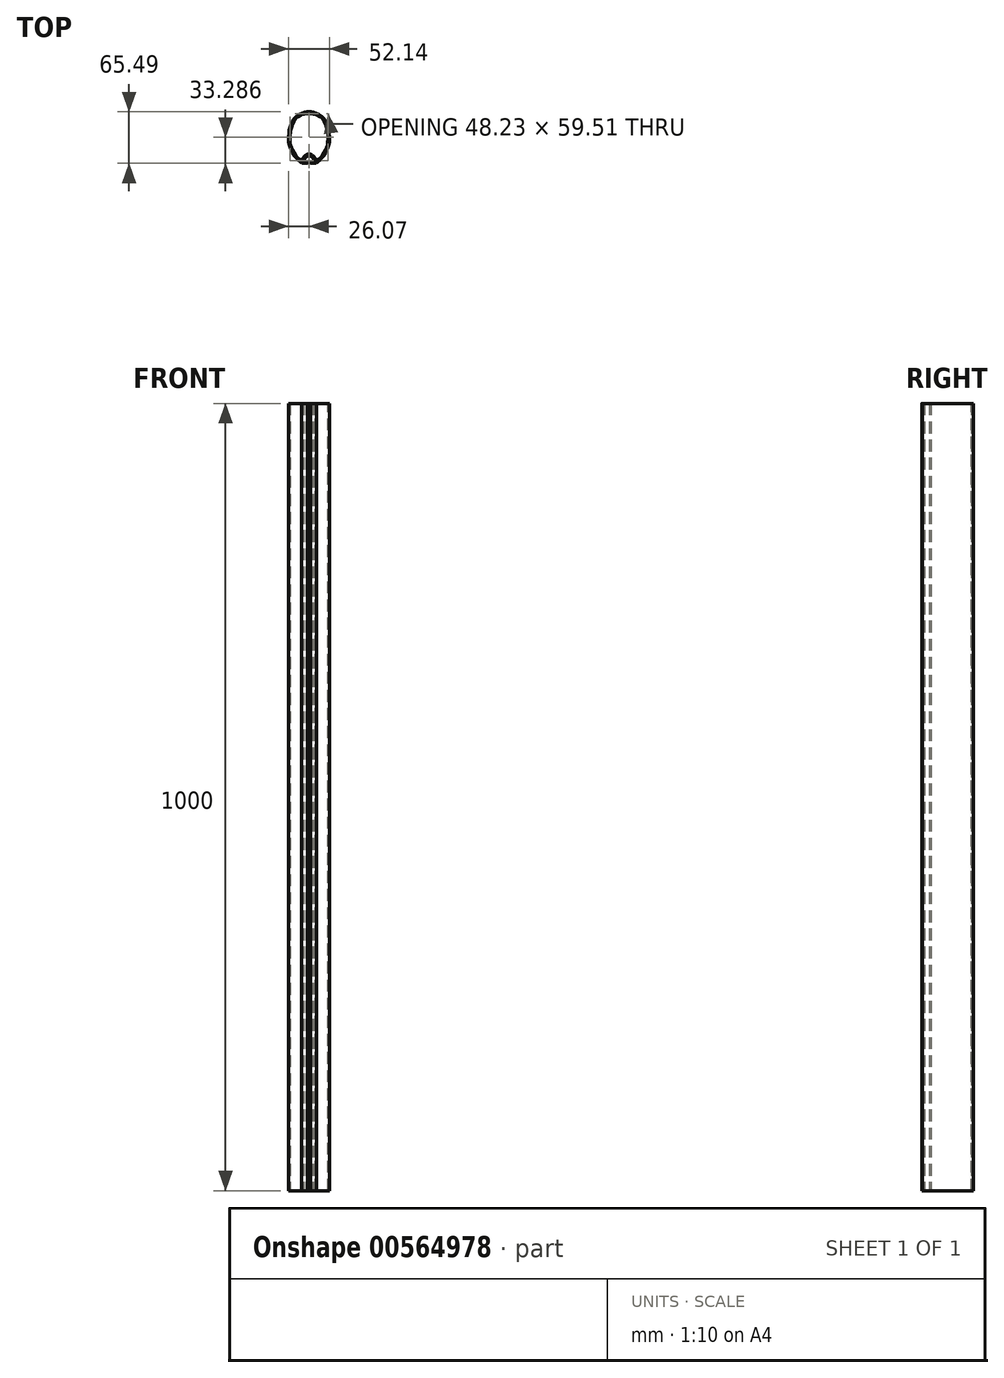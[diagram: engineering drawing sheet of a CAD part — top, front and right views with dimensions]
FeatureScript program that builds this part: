
annotation { "Feature Type Name" : "Feature", "Feature Type Description" : "" }
export const myFeature = defineFeature(function(context is Context, id is Id, definition is map)
    precondition{}
    {
        {
            var Q0;
            Q0=qCreatedBy(makeId("Top.planeOp"),FACE);
            var sketch = newSketch(context, id + "F0", { "sketchPlane" : qUnion([Q0])});
            skPoint(sketch, "E0", {"position": v(0, 8.5) * mm});
            skSolve(sketch);
        }
        {
            var Q0;
            Q0=qCreatedBy(makeId("Top.planeOp"),FACE);
            var sketch = newSketch(context, id + "F1", { "sketchPlane" : qUnion([Q0])});
            skPoint(sketch, "E1", {"position": v(0, -1.5) * mm});
            skSolve(sketch);
        }
        {
            var Q0;
            Q0=qCreatedBy(makeId("Top.planeOp"),FACE);
            var sketch = newSketch(context, id + "F2", { "sketchPlane" : qUnion([Q0])});
            skPoint(sketch, "E2", {"position": v(-13, 0) * mm});
            skSolve(sketch);
        }
        {
            var Q0;
            Q0=qCreatedBy(makeId("Top.planeOp"),FACE);
            var sketch = newSketch(context, id + "F3", { "sketchPlane" : qUnion([Q0])});
            skPoint(sketch, "E3", {"position": v(-20.75, 0) * mm});
            skSolve(sketch);
        }
        {
            var Q0;
            Q0=qCreatedBy(makeId("Top.planeOp"),FACE);
            var sketch = newSketch(context, id + "F4", { "sketchPlane" : qUnion([Q0])});
            skLineSegment(sketch, "E4", {"start": v(-20.75, 0) * mm, "end": v(-20.75, 0.34) * mm});
            skSolve(sketch);
        }
        {
            var Q0;
            Q0=qCreatedBy(makeId("Top.planeOp"),FACE);
            var sketch = newSketch(context, id + "F5", { "sketchPlane" : qUnion([Q0])});
            skPoint(sketch, "E5", {"position": v(-20.75, 0.34) * mm});
            skSolve(sketch);
        }
        {
            var Q0;
            Q0=qCreatedBy(makeId("Top.planeOp"),FACE);
            var sketch = newSketch(context, id + "F6", { "sketchPlane" : qUnion([Q0])});
            skPoint(sketch, "E6", {"position": v(0, -32.5) * mm});
            skSolve(sketch);
        }
        {
            var Q0;
            Q0=qCreatedBy(makeId("Top.planeOp"),FACE);
            var sketch = newSketch(context, id + "F7", { "sketchPlane" : qUnion([Q0])});
            skPoint(sketch, "E7", {"position": v(0, -22.83) * mm});
            skSolve(sketch);
        }
        {
            var Q0;
            Q0=qCreatedBy(makeId("Top.planeOp"),FACE);
            var sketch = newSketch(context, id + "F8", { "sketchPlane" : qUnion([Q0])});
            skPoint(sketch, "E8", {"position": v(0, -27.83) * mm});
            skSolve(sketch);
        }
        {
            var Q0;
            Q0=qCreatedBy(makeId("Top.planeOp"),FACE);
            var sketch = newSketch(context, id + "F9", { "sketchPlane" : qUnion([Q0])});
            skCircle(sketch, "E9", {"center": v(0, -27.83) * mm, "radius": 5 * mm});
            skSolve(sketch);
        }
        {
            var Q0;
            Q0=qCreatedBy(makeId("Top.planeOp"),FACE);
            var sketch = newSketch(context, id + "F10", { "sketchPlane" : qUnion([Q0])});
            skCircle(sketch, "E10", {"center": v(0, -27.83) * mm, "radius": 7.25 * mm});
            skSolve(sketch);
        }
        {
            var Q0;
            Q0=qCreatedBy(makeId("Top.planeOp"),FACE);
            var sketch = newSketch(context, id + "F11", { "sketchPlane" : qUnion([Q0])});
            skLineSegment(sketch, "E11", {"start": v(-2.11, -14.04) * mm, "end": v(17.17, -37.02) * mm});
            skSolve(sketch);
        }
        {
            var Q0;
            Q0=qCreatedBy(makeId("Top.planeOp"),FACE);
            var sketch = newSketch(context, id + "F12", { "sketchPlane" : qUnion([Q0])});
            skLineSegment(sketch, "E12", {"start": v(-4.06, -15.22) * mm, "end": v(15.2, -38.17) * mm});
            skSolve(sketch);
        }
        {
            var Q0;
            Q0=qCreatedBy(makeId("Top.planeOp"),FACE);
            var sketch = newSketch(context, id + "F13", { "sketchPlane" : qUnion([Q0])});
            skPoint(sketch, "E13", {"position": v(3.83, -24.62) * mm});
            skSolve(sketch);
        }
        {
            var Q0;
            Q0=qCreatedBy(makeId("Top.planeOp"),FACE);
            var sketch = newSketch(context, id + "F14", { "sketchPlane" : qUnion([Q0])});
            skPoint(sketch, "E14", {"position": v(5.55, -23.17) * mm});
            skSolve(sketch);
        }
        {
            var Q0;
            Q0=qCreatedBy(makeId("Top.planeOp"),FACE);
            var sketch = newSketch(context, id + "F15", { "sketchPlane" : qUnion([Q0])});
            skPoint(sketch, "E15", {"position": v(0, -20.58) * mm});
            skSolve(sketch);
        }
        {
            var Q0;
            Q0=qCreatedBy(makeId("Top.planeOp"),FACE);
            var sketch = newSketch(context, id + "F16", { "sketchPlane" : qUnion([Q0])});
            skArc(sketch, "E16", {"start": v(0, -20.58) * mm, "mid": v(3.06, -21.26) * mm, "end": v(5.55, -23.17) * mm});
            skSolve(sketch);
        }
        {
            var Q0;
            Q0=qCreatedBy(makeId("Top.planeOp"),FACE);
            var sketch = newSketch(context, id + "F17", { "sketchPlane" : qUnion([Q0])});
            skArc(sketch, "E17", {"start": v(0, -22.83) * mm, "mid": v(2.11, -23.3) * mm, "end": v(3.83, -24.62) * mm});
            skSolve(sketch);
        }
        {
            var Q0;
            Q0=qCreatedBy(makeId("Top.planeOp"),FACE);
            var sketch = newSketch(context, id + "F18", { "sketchPlane" : qUnion([Q0])});
            skLineSegment(sketch, "E18", {"start": v(0, -20.58) * mm, "end": v(0, -22.83) * mm});
            skSolve(sketch);
        }
        {
            var Q0;
            Q0=qCreatedBy(makeId("Top.planeOp"),FACE);
            var sketch = newSketch(context, id + "F19", { "sketchPlane" : qUnion([Q0])});
            skPoint(sketch, "E19", {"position": v(0, 33) * mm});
            skSolve(sketch);
        }
        {
            var Q0;
            Q0=qCreatedBy(makeId("Top.planeOp"),FACE);
            var sketch = newSketch(context, id + "F20", { "sketchPlane" : qUnion([Q0])});
            skCircle(sketch, "E20", {"center": v(-13, 0) * mm, "radius": 37.25 * mm});
            skSolve(sketch);
        }
        {
            var Q0;
            Q0=qCreatedBy(makeId("Top.planeOp"),FACE);
            var sketch = newSketch(context, id + "F21", { "sketchPlane" : qUnion([Q0])});
            skPoint(sketch, "E21", {"position": v(8.62, -30.33) * mm});
            skSolve(sketch);
        }
        {
            var Q0;
            Q0=qCreatedBy(makeId("Top.planeOp"),FACE);
            var sketch = newSketch(context, id + "F22", { "sketchPlane" : qUnion([Q0])});
            skPoint(sketch, "E22", {"position": v(10.42, -28.97) * mm});
            skSolve(sketch);
        }
        {
            var Q0;
            Q0=qCreatedBy(makeId("Top.planeOp"),FACE);
            var sketch = newSketch(context, id + "F23", { "sketchPlane" : qUnion([Q0])});
            skPoint(sketch, "E23", {"position": v(6.65, -26.5) * mm});
            skSolve(sketch);
        }
        {
            var Q0;
            Q0=qCreatedBy(makeId("Top.planeOp"),FACE);
            var sketch = newSketch(context, id + "F24", { "sketchPlane" : qUnion([Q0])});
            skLineSegment(sketch, "E24.bottom", {"start": v(0, -32.5) * mm, "end": v(1.75, -32.5) * mm});
            skLineSegment(sketch, "E24.top", {"start": v(0, -31) * mm, "end": v(1.75, -31) * mm});
            skLineSegment(sketch, "E24.left", {"start": v(0, -32.5) * mm, "end": v(0, -31) * mm});
            skLineSegment(sketch, "E24.right", {"start": v(1.75, -32.5) * mm, "end": v(1.75, -31) * mm});
            skSolve(sketch);
        }
        {
            var Q0;
            Q0=qCreatedBy(makeId("Top.planeOp"),FACE);
            var sketch = newSketch(context, id + "F25", { "sketchPlane" : qUnion([Q0])});
            skLineSegment(sketch, "E25.bottom", {"start": v(1.75, -32.5) * mm, "end": v(6.65, -32.5) * mm});
            skLineSegment(sketch, "E25.top", {"start": v(1.75, -31) * mm, "end": v(6.65, -31) * mm});
            skLineSegment(sketch, "E25.left", {"start": v(1.75, -32.5) * mm, "end": v(1.75, -31) * mm});
            skLineSegment(sketch, "E25.right", {"start": v(6.65, -32.5) * mm, "end": v(6.65, -31) * mm});
            skSolve(sketch);
        }
        {
            var Q0;
            Q0=qCreatedBy(makeId("Top.planeOp"),FACE);
            var sketch = newSketch(context, id + "F26", { "sketchPlane" : qUnion([Q0])});
            skArc(sketch, "E26", {"start": v(9.68, -31.68) * mm, "mid": v(8.22, -32.3) * mm, "end": v(6.65, -32.5) * mm});
            skSolve(sketch);
        }
        {
            var Q0;
            Q0=qCreatedBy(makeId("Top.planeOp"),FACE);
            var sketch = newSketch(context, id + "F27", { "sketchPlane" : qUnion([Q0])});
            skFitSpline(sketch, "E27", {"points": [v(10.42, -28.97) * mm, v(14.17, -25.46) * mm, v(16.96, -22.08) * mm, v(19.62, -17.98) * mm, v(21.39, -14.28) * mm, v(22.82, -10.41) * mm, v(23.66, -6.65) * mm, v(24.1, -3.42) * mm, v(24.24, 0) * mm, v(24.09, 3.46) * mm, v(23.7, 6.94) * mm, v(22.76, 11.67) * mm, v(21.35, 16.22) * mm, v(19.88, 19.59) * mm, v(16.38, 24.28) * mm, v(13.4, 26.83) * mm, v(10.3, 28.77) * mm, v(9.78, 28.98) * mm, v(9.04, 29.21) * mm, v(4.04, 30.3) * mm, v(0, 30.54) * mm], "startDerivative": vector(65.68, 55.9) * mm, "endDerivative": vector(-74.77, 3.53) * mm});
            skSolve(sketch);
        }
        {
            var Q0;
            Q0=qCreatedBy(makeId("Top.planeOp"),FACE);
            var sketch = newSketch(context, id + "F28", { "sketchPlane" : qUnion([Q0])});
            skFitSpline(sketch, "E28", {"points": [v(9.68, -31.68) * mm, v(10.28, -31.25) * mm, v(11.63, -30.22) * mm, v(15.66, -26.5) * mm, v(18.52, -23) * mm, v(21.18, -18.81) * mm, v(23.06, -14.82) * mm, v(24.5, -10.77) * mm, v(25.41, -6.88) * mm, v(25.87, -3.56) * mm, v(26, 0) * mm, v(25.84, 3.56) * mm, v(25.45, 7.22) * mm, v(24.5, 11.98) * mm, v(23.06, 16.71) * mm, v(21.46, 20.28) * mm, v(17.69, 25.4) * mm, v(14.4, 28.3) * mm, v(10.61, 30.57) * mm, v(7.6, 31.76) * mm, v(3.98, 32.66) * mm, v(0, 33) * mm], "startDerivative": vector(25.9, 18.75) * mm, "endDerivative": vector(-83.26, 2.5) * mm});
            skSolve(sketch);
        }
        {
            var Q0;
            Q0=qCreatedBy(makeId("Top.planeOp"),FACE);
            var sketch = newSketch(context, id + "F29", { "sketchPlane" : qUnion([Q0])});
            skLineSegment(sketch, "E29", {"start": v(8.62, -30.33) * mm, "end": v(3.83, -24.62) * mm});
            skSolve(sketch);
        }
        {
            var Q0;
            Q0=qCreatedBy(makeId("Top.planeOp"),FACE);
            var sketch = newSketch(context, id + "F30", { "sketchPlane" : qUnion([Q0])});
            skLineSegment(sketch, "E30", {"start": v(5.55, -23.17) * mm, "end": v(10.42, -28.97) * mm});
            skSolve(sketch);
        }
        {
            var Q0;
            Q0=qCreatedBy(makeId("Top.planeOp"),FACE);
            var sketch = newSketch(context, id + "F31", { "sketchPlane" : qUnion([Q0])});
            skPoint(sketch, "E31", {"position": v(2.75, -31.5) * mm});
            skSolve(sketch);
        }
        {
            var Q0;
            Q0=qCreatedBy(makeId("Top.planeOp"),FACE);
            var sketch = newSketch(context, id + "F32", { "sketchPlane" : qUnion([Q0])});
            skArc(sketch, "E32", {"start": v(2.75, -32.5) * mm, "mid": v(1.88, -31) * mm, "end": v(3.62, -31) * mm});
            skSolve(sketch);
        }
        {
            var Q0;
            Q0=qCreatedBy(makeId("Top.planeOp"),FACE);
            var sketch = newSketch(context, id + "F33", { "sketchPlane" : qUnion([Q0])});
            skFitSpline(sketch, "E33", {"points": [v(6.65, -31) * mm, v(7.55, -30.97) * mm, v(8.25, -30.82) * mm, v(8.52, -30.56) * mm, v(8.47, -30.14) * mm], "startDerivative": vector(2.94, 0.03) * mm, "endDerivative": vector(-1.7, 2.33) * mm});
            skSolve(sketch);
        }
        {
            var Q0;
            Q0=qCreatedBy(makeId("Top.planeOp"),FACE);
            var sketch = newSketch(context, id + "F34", { "sketchPlane" : qUnion([Q0])});
            skLineSegment(sketch, "E34", {"start": v(2.75, -32.5) * mm, "end": v(6.65, -32.5) * mm});
            skSolve(sketch);
        }
        {
            var Q0;
            Q0=qCreatedBy(makeId("Top.planeOp"),FACE);
            var sketch = newSketch(context, id + "F35", { "sketchPlane" : qUnion([Q0])});
            skLineSegment(sketch, "E35", {"start": v(3.62, -31) * mm, "end": v(6.65, -31) * mm});
            skSolve(sketch);
        }
        {
            var Q0;
            Q0=qCreatedBy(makeId("Top.planeOp"),FACE);
            var sketch = newSketch(context, id + "F36", { "sketchPlane" : qUnion([Q0])});
            skLineSegment(sketch, "E36", {"start": v(0, 33) * mm, "end": v(0, 30.54) * mm});
            skSolve(sketch);
        }
        {
            var Q0;
            Q0=qCreatedBy(makeId("Top.planeOp"),FACE);
            var sketch = newSketch(context, id + "F37", { "sketchPlane" : qUnion([Q0])});
            skLineSegment(sketch, "E37", {"start": v(23.55, 7.92) * mm, "end": v(23.55, -7.26) * mm});
            skSolve(sketch);
        }
        {
            var Q0;
            Q0=qCreatedBy(makeId("Top.planeOp"),FACE);
            var sketch = newSketch(context, id + "F38", { "sketchPlane" : qUnion([Q0])});
            skLineSegment(sketch, "E38.0", {"start": v(23.55, 7.92) * mm, "end": v(23.55, -7.26) * mm});
            skArc(sketch, "E39.0", {"start": v(0, -20.58) * mm, "mid": v(3.06, -21.26) * mm, "end": v(5.55, -23.17) * mm});
            skLineSegment(sketch, "E40.0", {"start": v(5.55, -23.17) * mm, "end": v(10.42, -28.97) * mm});
            skFitSpline(sketch, "E41.0", {"points": [v(10.42, -28.97) * mm, v(11.7, -27.87) * mm, v(14.28, -25.52) * mm, v(16.99, -22.17) * mm, v(19.73, -18.03) * mm, v(21.4, -14.32) * mm, v(22.92, -10.47) * mm, v(23.7, -6.67) * mm, v(24.15, -3.44) * mm, v(24.29, 0) * mm, v(24.11, 3.5) * mm, v(23.76, 6.99) * mm, v(22.88, 11.68) * mm, v(21.35, 16.27) * mm, v(20.12, 19.63) * mm, v(16.44, 24.51) * mm, v(13.71, 26.7) * mm, v(10.38, 28.8) * mm, v(9.77, 28.98) * mm, v(8.94, 29.28) * mm, v(3.79, 30.55) * mm, v(1.3, 30.48) * mm, v(0, 30.54) * mm]});
            skFitSpline(sketch, "E42.0", {"points": [v(9.68, -31.68) * mm, v(9.86, -31.55) * mm, v(10.36, -31.2) * mm, v(11.77, -30.18) * mm, v(15.9, -26.46) * mm, v(18.51, -23.1) * mm, v(21.3, -18.85) * mm, v(23.1, -14.87) * mm, v(24.58, -10.82) * mm, v(25.46, -6.9) * mm, v(25.93, -3.58) * mm, v(26.06, 0.01) * mm, v(25.85, 3.6) * mm, v(25.51, 7.28) * mm, v(24.6, 11.99) * mm, v(23.08, 16.79) * mm, v(21.68, 20.33) * mm, v(17.79, 25.62) * mm, v(14.6, 28.3) * mm, v(10.65, 30.68) * mm, v(7.64, 31.8) * mm, v(3.96, 32.8) * mm, v(1.34, 32.95) * mm, v(0, 33) * mm]});
            skArc(sketch, "E43.0", {"start": v(9.68, -31.68) * mm, "mid": v(8.22, -32.3) * mm, "end": v(6.65, -32.5) * mm});
            skLineSegment(sketch, "E44.0", {"start": v(2.75, -32.5) * mm, "end": v(6.65, -32.5) * mm});
            skArc(sketch, "E45.0", {"start": v(2.75, -32.5) * mm, "mid": v(1.88, -31) * mm, "end": v(3.62, -31) * mm});
            skLineSegment(sketch, "E46.0", {"start": v(3.62, -31) * mm, "end": v(6.65, -31) * mm});
            skFitSpline(sketch, "E47.0", {"points": [v(6.65, -31) * mm, v(6.95, -31) * mm, v(7.52, -30.99) * mm, v(8.25, -30.88) * mm, v(8.57, -30.58) * mm, v(8.59, -30.3) * mm, v(8.47, -30.14) * mm]});
            skLineSegment(sketch, "E48.0", {"start": v(8.62, -30.33) * mm, "end": v(3.83, -24.62) * mm});
            skArc(sketch, "E49.0", {"start": v(0, -22.83) * mm, "mid": v(2.11, -23.3) * mm, "end": v(3.83, -24.62) * mm});
            skLineSegment(sketch, "E50.0", {"start": v(0, 33) * mm, "end": v(0, 30.54) * mm});
            skLineSegment(sketch, "E51.0", {"start": v(0, -20.58) * mm, "end": v(0, -22.83) * mm});
            skSolve(sketch);
        }
        {
            var Q0;
            Q0 = qSketchRegion(id + "F38", true);
            extrude(context, id + "F39", {"entities" : qUnion([Q0]), "depth" : 1000 * mm, "offsetDistance" : 25 * mm, "symmetric" : true});
        }
        {
            var Q0;
            Q0=makeQuery(id+"F39.opExtrude","SWEPT_BODY",BODY,{"disambiguationData":[OSD([sQuery(id+"F38.wireOp",EDGE,"E38.0"),sQuery(id+"F38.wireOp",EDGE,"E39.0"),sQuery(id+"F38.wireOp",EDGE,"E40.0"),sQuery(id+"F38.wireOp",EDGE,"E41.0"),sQuery(id+"F38.wireOp",EDGE,"E42.0"),sQuery(id+"F38.wireOp",EDGE,"E43.0"),sQuery(id+"F38.wireOp",EDGE,"E44.0"),sQuery(id+"F38.wireOp",EDGE,"E45.0"),sQuery(id+"F38.wireOp",EDGE,"E46.0"),sQuery(id+"F38.wireOp",EDGE,"E47.0"),sQuery(id+"F38.wireOp",EDGE,"E48.0"),sQuery(id+"F38.wireOp",EDGE,"E49.0"),sQuery(id+"F38.wireOp",EDGE,"E50.0"),sQuery(id+"F38.wireOp",EDGE,"E51.0")])]});
            var Q1;
            Q1=qCreatedBy(makeId("Right.planeOp"),FACE);
            mirror(context, id + "F40", {"entities" : qUnion([Q0]), "mirrorPlane" : qUnion([Q1])});
        }
        {
            var Q0;
            Q0=makeQuery(id+"F39.opExtrude","SWEPT_BODY",BODY,{"disambiguationData":[OSD([sQuery(id+"F38.wireOp",EDGE,"E38.0"),sQuery(id+"F38.wireOp",EDGE,"E39.0"),sQuery(id+"F38.wireOp",EDGE,"E40.0"),sQuery(id+"F38.wireOp",EDGE,"E41.0"),sQuery(id+"F38.wireOp",EDGE,"E42.0"),sQuery(id+"F38.wireOp",EDGE,"E43.0"),sQuery(id+"F38.wireOp",EDGE,"E44.0"),sQuery(id+"F38.wireOp",EDGE,"E45.0"),sQuery(id+"F38.wireOp",EDGE,"E46.0"),sQuery(id+"F38.wireOp",EDGE,"E47.0"),sQuery(id+"F38.wireOp",EDGE,"E48.0"),sQuery(id+"F38.wireOp",EDGE,"E49.0"),sQuery(id+"F38.wireOp",EDGE,"E50.0"),sQuery(id+"F38.wireOp",EDGE,"E51.0")])]});
            var Q1;
            Q1=makeQuery(id+"F40.opPattern","COPY",BODY,{"derivedFrom":makeQuery(id+"F39.opExtrude","SWEPT_BODY",BODY,{"disambiguationData":[OSD([sQuery(id+"F38.wireOp",EDGE,"E38.0"),sQuery(id+"F38.wireOp",EDGE,"E39.0"),sQuery(id+"F38.wireOp",EDGE,"E40.0"),sQuery(id+"F38.wireOp",EDGE,"E41.0"),sQuery(id+"F38.wireOp",EDGE,"E42.0"),sQuery(id+"F38.wireOp",EDGE,"E43.0"),sQuery(id+"F38.wireOp",EDGE,"E44.0"),sQuery(id+"F38.wireOp",EDGE,"E45.0"),sQuery(id+"F38.wireOp",EDGE,"E46.0"),sQuery(id+"F38.wireOp",EDGE,"E47.0"),sQuery(id+"F38.wireOp",EDGE,"E48.0"),sQuery(id+"F38.wireOp",EDGE,"E49.0"),sQuery(id+"F38.wireOp",EDGE,"E50.0"),sQuery(id+"F38.wireOp",EDGE,"E51.0")])]}),"instanceName":"1"});
            booleanBodies(context, id + "F41", {"operationType" : BooleanOperationType.UNION, "tools" : qUnion([Q0, Q1])});
        }
    });
